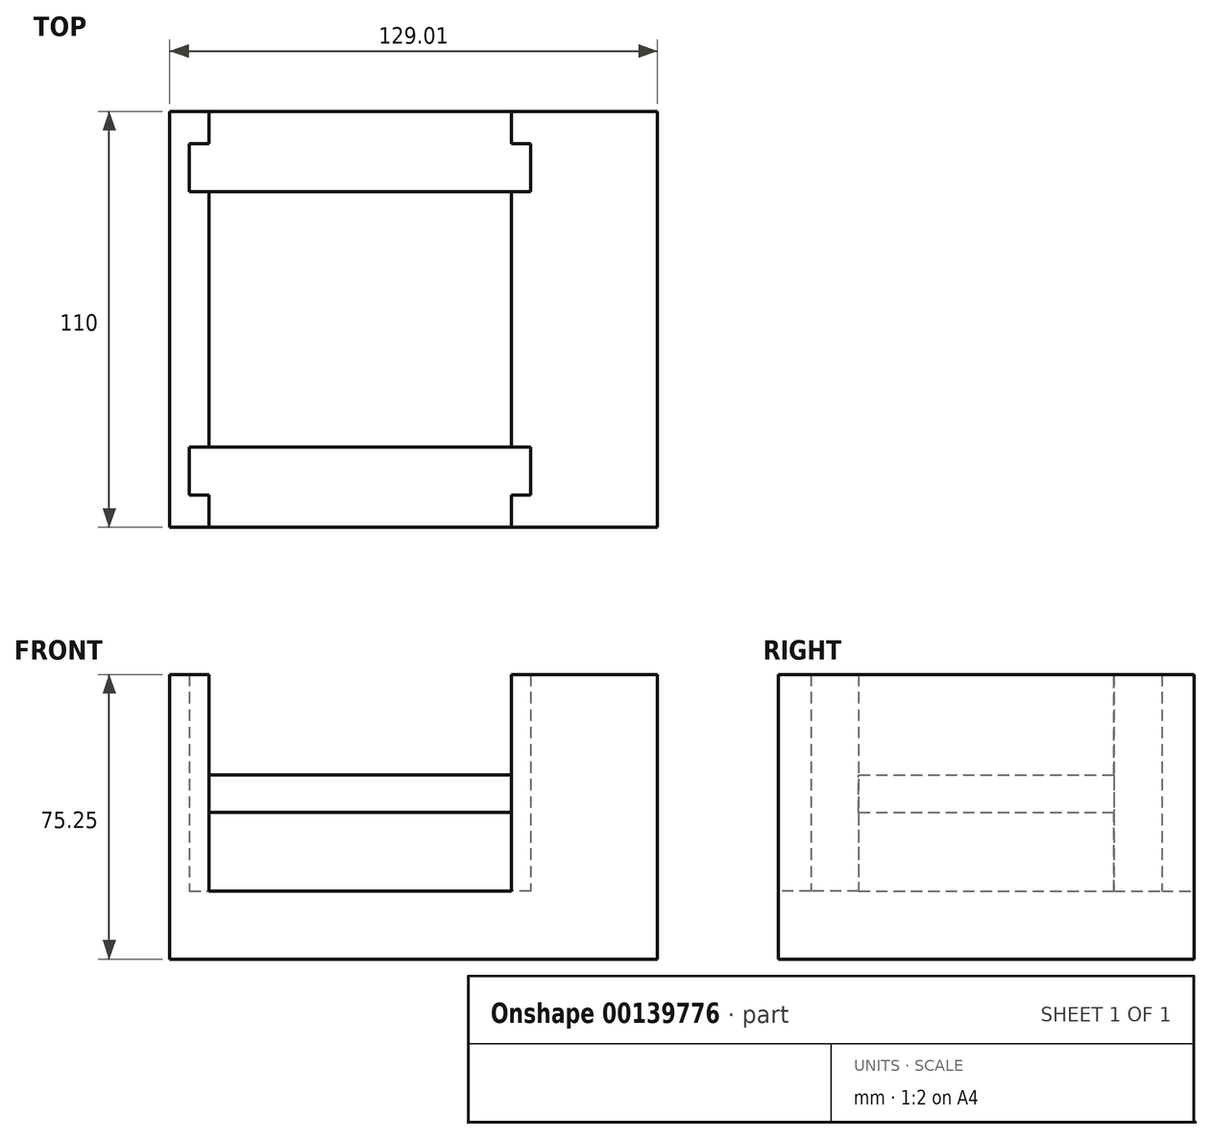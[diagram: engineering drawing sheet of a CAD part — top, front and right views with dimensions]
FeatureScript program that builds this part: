
annotation { "Feature Type Name" : "Feature", "Feature Type Description" : "" }
export const myFeature = defineFeature(function(context is Context, id is Id, definition is map)
    precondition{}
    {
        {
            var Q0;
            Q0=qCreatedBy(makeId("Top.planeOp"),FACE);
            var sketch = newSketch(context, id + "F0", { "sketchPlane" : qUnion([Q0])});
            skLineSegment(sketch, "E0.top", {"start": v(0, 68.76) * mm, "end": v(0, 68.76) * mm});
            skLineSegment(sketch, "E0.left", {"start": v(0, -68.76) * mm, "end": v(0, 68.76) * mm});
            skLineSegment(sketch, "E0.right", {"start": v(0, -68.76) * mm, "end": v(0, 68.76) * mm, "construction": true});
            skPoint(sketch, "E0.middle", {"position": v(0, 0) * mm});
            skLineSegment(sketch, "E1", {"start": v(-50.34, 55) * mm, "end": v(-40, 55) * mm});
            skLineSegment(sketch, "E2", {"start": v(-40, 55) * mm, "end": v(-40, 46.43) * mm});
            skLineSegment(sketch, "E3", {"start": v(-40, 46.43) * mm, "end": v(-45.17, 46.43) * mm});
            skLineSegment(sketch, "E4", {"start": v(-45.17, 46.43) * mm, "end": v(-45.17, 33.73) * mm});
            skLineSegment(sketch, "E5", {"start": v(-45.17, 33.73) * mm, "end": v(-40, 33.73) * mm});
            skLineSegment(sketch, "E6.bottom", {"start": v(85.9, 0) * mm, "end": v(-85.9, 0) * mm});
            skLineSegment(sketch, "E6.top", {"start": v(85.9, 0) * mm, "end": v(-85.9, 0) * mm, "construction": true});
            skLineSegment(sketch, "E6.left", {"start": v(85.9, 0) * mm, "end": v(85.9, 0) * mm});
            skLineSegment(sketch, "E6.right", {"start": v(-85.9, 0) * mm, "end": v(-85.9, 0) * mm});
            skLineSegment(sketch, "E7.MirrorCS", {"start": v(-45.17, -33.73) * mm, "end": v(-40, -33.73) * mm});
            skLineSegment(sketch, "E8.MirrorCS", {"start": v(-40, -46.43) * mm, "end": v(-45.17, -46.43) * mm});
            skLineSegment(sketch, "E9.MirrorCS", {"start": v(-45.17, -46.43) * mm, "end": v(-45.17, -33.73) * mm});
            skLineSegment(sketch, "E10.MirrorCS", {"start": v(-40, -55) * mm, "end": v(-40, -46.43) * mm});
            skLineSegment(sketch, "E11.MirrorCS", {"start": v(-50.34, -55) * mm, "end": v(-40, -55) * mm});
            skLineSegment(sketch, "E12", {"start": v(-50.34, 55) * mm, "end": v(-50.34, -55) * mm});
            skLineSegment(sketch, "E13", {"start": v(-40, 33.73) * mm, "end": v(-40, -33.73) * mm});
            skLineSegment(sketch, "E14.MirrorCS", {"start": v(45.17, -33.73) * mm, "end": v(40, -33.73) * mm});
            skLineSegment(sketch, "E15.MirrorCS", {"start": v(45.17, 33.73) * mm, "end": v(40, 33.73) * mm});
            skLineSegment(sketch, "E16.MirrorCS", {"start": v(40, -46.43) * mm, "end": v(45.17, -46.43) * mm});
            skLineSegment(sketch, "E17.MirrorCS", {"start": v(40, 46.43) * mm, "end": v(45.17, 46.43) * mm});
            skLineSegment(sketch, "E18.MirrorCS", {"start": v(45.17, 46.43) * mm, "end": v(45.17, 33.73) * mm});
            skLineSegment(sketch, "E19.MirrorCS", {"start": v(45.17, -46.43) * mm, "end": v(45.17, -33.73) * mm});
            skLineSegment(sketch, "E20.MirrorCS", {"start": v(40, -55) * mm, "end": v(40, -46.43) * mm});
            skLineSegment(sketch, "E21.MirrorCS", {"start": v(40, 33.73) * mm, "end": v(40, -33.73) * mm});
            skLineSegment(sketch, "E22.MirrorCS", {"start": v(50.34, 55) * mm, "end": v(40, 55) * mm});
            skLineSegment(sketch, "E23.MirrorCS", {"start": v(50.34, 55) * mm, "end": v(50.34, -55) * mm});
            skLineSegment(sketch, "E24.MirrorCS", {"start": v(50.34, -55) * mm, "end": v(40, -55) * mm});
            skLineSegment(sketch, "E25.MirrorCS", {"start": v(40, 55) * mm, "end": v(40, 46.43) * mm});
            skLineSegment(sketch, "E26", {"start": v(-40, 55) * mm, "end": v(40, 55) * mm});
            skLineSegment(sketch, "E27", {"start": v(-40, -55) * mm, "end": v(40, -55) * mm});
            skSolve(sketch);
        }
        {
            var Q0;
            Q0=qSketchRegion(id+"F0",true);
            extrude(context, id + "F1", {"entities" : qUnion([Q0]), "depth" : 17.93 * mm});
        }
        {
            var Q0;
            {var subQ1=sQuery(id+"F0.wireOp",EDGE,"E14.MirrorCS");Q0=makeQuery(id+"F0.imprint","IMPRINT",FACE,{"disambiguationData":[TD([[makeQuery(id+"F0.imprint","IMPRINT",EDGE,{"derivedFrom":subQ1}),-1.0]])]});}
            var Q1;
            {var subQ0=sQuery(id+"F0.wireOp",EDGE,"E7.MirrorCS");Q1=makeQuery(id+"F0.imprint","IMPRINT",FACE,{"disambiguationData":[TD([[makeQuery(id+"F0.imprint","IMPRINT",EDGE,{"derivedFrom":subQ0}),1.0]])]});}
            var Q2;
            {var subQ5=sQuery(id+"F0.wireOp",EDGE,"E1");Q2=makeQuery(id+"F0.imprint","IMPRINT",FACE,{"disambiguationData":[TD([[makeQuery(id+"F0.imprint","IMPRINT",EDGE,{"derivedFrom":subQ5}),-1.0]])]});}
            var Q3;
            {var subQ6=sQuery(id+"F0.wireOp",EDGE,"E15.MirrorCS");Q3=makeQuery(id+"F0.imprint","IMPRINT",FACE,{"disambiguationData":[TD([[makeQuery(id+"F0.imprint","IMPRINT",EDGE,{"derivedFrom":subQ6}),1.0]])]});}
            extrude(context, id + "F2", {"entities" : qUnion([Q0, Q1, Q2, Q3]), "operationType" : NewBodyOperationType.ADD, "depth" : 75.25 * mm});
        }
        {
            var Q0;
            Q0=qCreatedBy(makeId("Front.planeOp"),FACE);
            var sketch = newSketch(context, id + "F3", { "sketchPlane" : qUnion([Q0])});
            skLineSegment(sketch, "E28.0", {"start": v(-40, 75.25) * mm, "end": v(-40, 17.93) * mm});
            skLineSegment(sketch, "E29.0", {"start": v(40, 75.25) * mm, "end": v(40, 17.93) * mm});
            skLineSegment(sketch, "E30.0", {"start": v(40, 17.93) * mm, "end": v(-40, 17.93) * mm});
            skLineSegment(sketch, "E31", {"start": v(-40, 38.86) * mm, "end": v(40, 38.86) * mm});
            skLineSegment(sketch, "E32", {"start": v(-40, 48.72) * mm, "end": v(40, 48.72) * mm});
            skSolve(sketch);
        }
        {
            var Q0;
            {var subQ0=sQuery(id+"F3.wireOp",EDGE,"E31");Q0=makeQuery(id+"F3.imprint","IMPRINT",FACE,{"disambiguationData":[TD([[makeQuery(id+"F3.imprint","IMPRINT",EDGE,{"derivedFrom":subQ0}),1.0]])]});}
            extrude(context, id + "F4", {"entities" : qUnion([Q0]), "operationType" : NewBodyOperationType.ADD, "endBound" : BoundingType.SYMMETRIC, "depth" : 67.46 * mm});
        }
        {
            var Q0;
            {var subQ0=sQuery(id+"F0.wireOp",EDGE,"E23.MirrorCS");Q0=makeQuery(id+"F2.boolean.opBoolean","MERGE",FACE,{"derivedFrom":[makeQuery(id+"F1.opExtrude","SWEPT_FACE",FACE,{"disambiguationData":[OSD([subQ0])]}),makeQuery(id+"F2.opExtrude","SWEPT_FACE",FACE,{"disambiguationData":[OSD([subQ0])]})]});}
            extrude(context, id + "F5", {"entities" : qUnion([Q0]), "operationType" : NewBodyOperationType.ADD, "depth" : 28.33 * mm});
        }
    });
